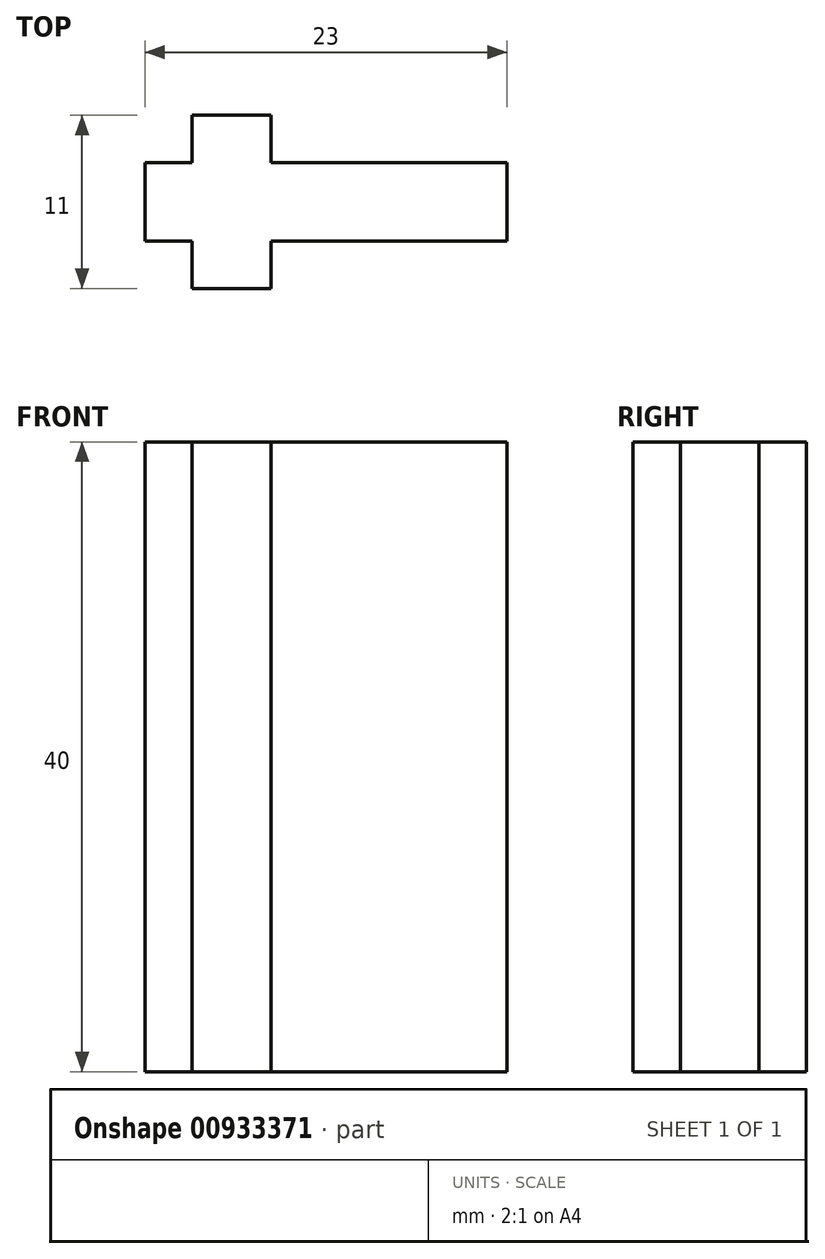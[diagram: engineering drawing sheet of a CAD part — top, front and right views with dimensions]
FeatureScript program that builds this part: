
annotation { "Feature Type Name" : "Feature", "Feature Type Description" : "" }
export const myFeature = defineFeature(function(context is Context, id is Id, definition is map)
    precondition{}
    {
        {
            var Q0;
            Q0=qCreatedBy(makeId("Top.planeOp"),FACE);
            var sketch = newSketch(context, id + "F0", { "sketchPlane" : qUnion([Q0])});
            skLineSegment(sketch, "E0.bottom", {"start": v(2.5, -5.5) * mm, "end": v(-2.5, -5.5) * mm});
            skLineSegment(sketch, "E0.top", {"start": v(2.5, 5.5) * mm, "end": v(-2.5, 5.5) * mm});
            skLineSegment(sketch, "E0.left", {"start": v(2.5, -5.5) * mm, "end": v(2.5, 5.5) * mm});
            skLineSegment(sketch, "E0.right", {"start": v(-2.5, -5.5) * mm, "end": v(-2.5, 5.5) * mm});
            skPoint(sketch, "E0.middle", {"position": v(0, 0) * mm});
            skLineSegment(sketch, "E1.bottom", {"start": v(5.5, -2.5) * mm, "end": v(-5.5, -2.5) * mm});
            skLineSegment(sketch, "E1.top", {"start": v(5.5, 2.5) * mm, "end": v(-5.5, 2.5) * mm});
            skLineSegment(sketch, "E1.left", {"start": v(5.5, -2.5) * mm, "end": v(5.5, 2.5) * mm});
            skLineSegment(sketch, "E1.right", {"start": v(-5.5, -2.5) * mm, "end": v(-5.5, 2.5) * mm});
            skLineSegment(sketch, "E2.bottom", {"start": v(2.5, -2.5) * mm, "end": v(17.5, -2.5) * mm});
            skLineSegment(sketch, "E2.top", {"start": v(2.5, 2.5) * mm, "end": v(17.5, 2.5) * mm});
            skLineSegment(sketch, "E2.left", {"start": v(2.5, -2.5) * mm, "end": v(2.5, 2.5) * mm});
            skLineSegment(sketch, "E2.right", {"start": v(17.5, -2.5) * mm, "end": v(17.5, 2.5) * mm});
            skSolve(sketch);
        }
        {
            var Q0;
            {var subQ0=sQuery(id+"F0.wireOp",EDGE,"E0.top");Q0=makeQuery(id+"F0.imprint","IMPRINT",FACE,{"disambiguationData":[TD([[makeQuery(id+"F0.imprint","IMPRINT",EDGE,{"derivedFrom":subQ0}),1.0]])]});}
            var Q1;
            {var subQ0=sQuery(id+"F0.wireOp",EDGE,"E1.bottom");var subQ1=sQuery(id+"F0.wireOp",EDGE,"E0.left");var subQ2=makeQuery(id+"F0.imprint","INTERSECT",VERTEX,{"derivedFrom":[subQ1,subQ0]});Q1=makeQuery(id+"F0.imprint","IMPRINT",FACE,{"disambiguationData":[TD([[makeQuery(id+"F0.imprint","IMPRINT",EDGE,{"disambiguationData":[TD([[subQ2,-1.0]])],"derivedFrom":subQ1}),1.0]])]});}
            var Q2;
            {var subQ5=sQuery(id+"F0.wireOp",EDGE,"E1.right");Q2=makeQuery(id+"F0.imprint","IMPRINT",FACE,{"disambiguationData":[TD([[makeQuery(id+"F0.imprint","IMPRINT",EDGE,{"derivedFrom":subQ5}),-1.0]])]});}
            var Q3;
            {var subQ0=sQuery(id+"F0.wireOp",EDGE,"E0.bottom");Q3=makeQuery(id+"F0.imprint","IMPRINT",FACE,{"disambiguationData":[TD([[makeQuery(id+"F0.imprint","IMPRINT",EDGE,{"derivedFrom":subQ0}),-1.0]])]});}
            var Q4;
            {var subQ5=sQuery(id+"F0.wireOp",EDGE,"E1.left");Q4=makeQuery(id+"F0.imprint","IMPRINT",FACE,{"disambiguationData":[TD([[makeQuery(id+"F0.imprint","IMPRINT",EDGE,{"derivedFrom":subQ5}),1.0]])]});}
            var Q5;
            Q5=makeQuery(id+"F0.imprint","IMPRINT",FACE,{"disambiguationData":[TD([[makeQuery(id+"F0.imprint","IMPRINT",EDGE,{"derivedFrom":sQuery(id+"F0.wireOp",EDGE,"E1.left")}),-1.0]])]});
            extrude(context, id + "F1", {"entities" : qUnion([Q0, Q1, Q2, Q3, Q4, Q5]), "depth" : 40 * mm, "offsetDistance" : 25 * mm});
        }
    });
